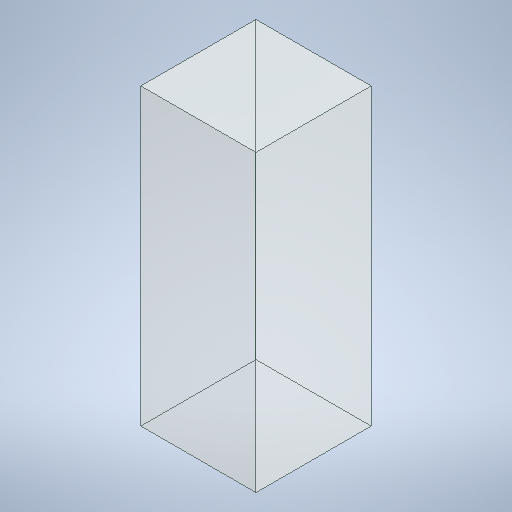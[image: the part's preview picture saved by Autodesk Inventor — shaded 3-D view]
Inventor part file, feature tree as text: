
AUTODESK INVENTOR PART (.ipt)
format: ipt  version: 2025.1 (Build 291241020, 241B)  size: 238,080 bytes
history: native  units: in
note: dims shown in document units (in); Inventor stores cm internally (conversion verified against a paired STEP export)
features: extrude x1, sketch x1
ambient origin geometry x8: Origin, YZ Plane, XZ Plane, XY Plane, X Axis, Y Axis, Z Axis, Center Point
bodies: Solid1 (feature_tree)
feature tree (2):
  extrude  "Extrusion1"  Depth=14.0in
  sketch  "Sketch1"  dims[d1=35.8128in d2=0.0in d3=14.0in]
